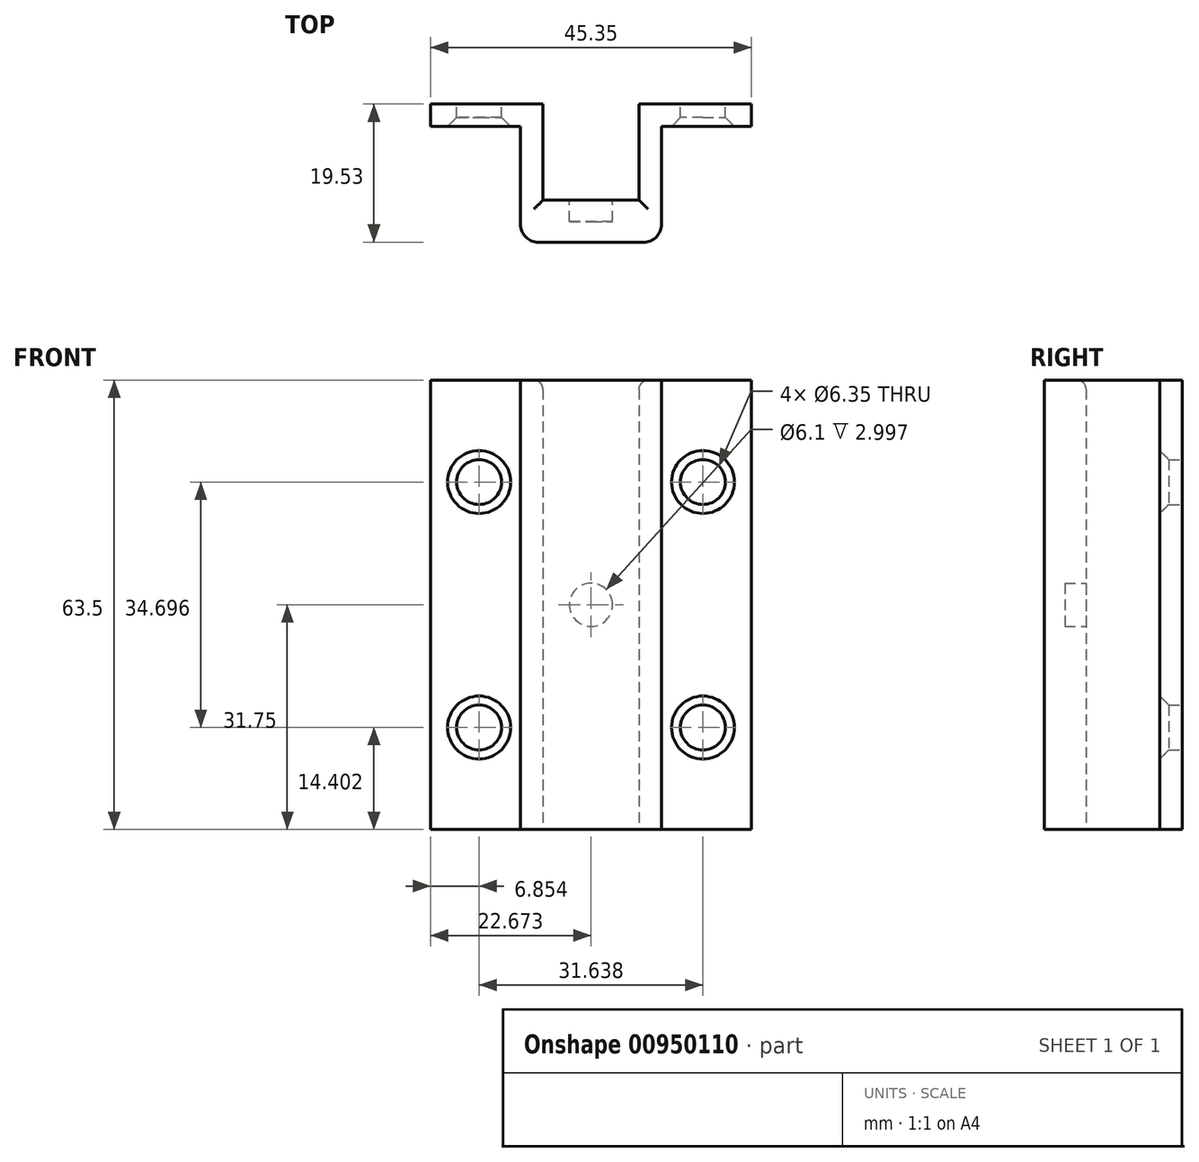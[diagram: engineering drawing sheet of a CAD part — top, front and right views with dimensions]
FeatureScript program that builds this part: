
annotation { "Feature Type Name" : "Feature", "Feature Type Description" : "" }
export const myFeature = defineFeature(function(context is Context, id is Id, definition is map)
    precondition{}
    {
        {
            var Q0;
            Q0=qCreatedBy(makeId("Top.planeOp"),FACE);
            var sketch = newSketch(context, id + "F0", { "sketchPlane" : qUnion([Q0])});
            skLineSegment(sketch, "E0", {"start": v(-9.03, 0) * mm, "end": v(4.58, 0) * mm});
            skLineSegment(sketch, "E1", {"start": v(-9.03, 0) * mm, "end": v(-9.03, 13.6) * mm});
            skLineSegment(sketch, "E2", {"start": v(4.58, 0) * mm, "end": v(4.58, 13.6) * mm});
            skLineSegment(sketch, "E3", {"start": v(4.58, 13.6) * mm, "end": v(20.45, 13.6) * mm});
            skLineSegment(sketch, "E4", {"start": v(20.45, 13.6) * mm, "end": v(20.45, 10.42) * mm});
            skLineSegment(sketch, "E5", {"start": v(20.45, 10.42) * mm, "end": v(7.75, 10.42) * mm});
            skLineSegment(sketch, "E6", {"start": v(7.75, 10.42) * mm, "end": v(7.75, -5.93) * mm});
            skLineSegment(sketch, "E7", {"start": v(7.75, -5.93) * mm, "end": v(-12.2, -5.93) * mm});
            skLineSegment(sketch, "E8", {"start": v(-9.03, 13.6) * mm, "end": v(-24.9, 13.6) * mm});
            skLineSegment(sketch, "E9", {"start": v(-24.9, 13.6) * mm, "end": v(-24.9, 10.42) * mm});
            skLineSegment(sketch, "E10", {"start": v(-24.9, 10.42) * mm, "end": v(-12.2, 10.42) * mm});
            skLineSegment(sketch, "E11", {"start": v(-12.2, 10.42) * mm, "end": v(-12.2, -5.93) * mm});
            skSolve(sketch);
        }
        {
            var Q0;
            Q0 = qSketchRegion(id + "F0", true);
            extrude(context, id + "F1", {"entities" : qUnion([Q0]), "depth" : 63.5 * mm, "offsetDistance" : 25.4 * mm});
        }
        {
            var Q0;
            Q0=makeQuery(id+"F1.opExtrude","SWEPT_FACE",FACE,{"disambiguationData":[OSD([sQuery(id+"F0.wireOp",EDGE,"E0")])]});
            var sketch = newSketch(context, id + "F2", { "sketchPlane" : qUnion([Q0])});
            skCircle(sketch, "E12", {"center": v(2.23, 31.75) * mm, "radius": 3.05 * mm});
            skPoint(sketch, "E13.orphan", {"position": v(-4.58, 31.75) * mm});
            skPoint(sketch, "E14.end.orphan", {"position": v(9.03, 31.75) * mm});
            skSolve(sketch);
        }
        {
            var Q0;
            Q0 = qSketchRegion(id + "F2", true);
            extrude(context, id + "F3", {"entities" : qUnion([Q0]), "operationType" : NewBodyOperationType.REMOVE, "oppositeDirection" : true, "depth" : 3 * mm, "offsetDistance" : 25.4 * mm});
        }
        {
            var Q0;
            Q0=makeQuery(id+"F1.opExtrude","SWEPT_FACE",FACE,{"disambiguationData":[OSD([sQuery(id+"F0.wireOp",EDGE,"E8")])]});
            var sketch = newSketch(context, id + "F4", { "sketchPlane" : qUnion([Q0])});
            skCircle(sketch, "E15", {"center": v(18.05, 49.1) * mm, "radius": 3.18 * mm});
            skCircle(sketch, "E16", {"center": v(18.05, 14.4) * mm, "radius": 3.18 * mm});
            skSolve(sketch);
        }
        {
            var Q0;
            Q0=makeQuery(id+"F1.opExtrude","SWEPT_FACE",FACE,{"disambiguationData":[OSD([sQuery(id+"F0.wireOp",EDGE,"E3")])]});
            var sketch = newSketch(context, id + "F5", { "sketchPlane" : qUnion([Q0])});
            skCircle(sketch, "E17", {"center": v(-13.6, 49.1) * mm, "radius": 3.18 * mm});
            skCircle(sketch, "E18", {"center": v(-13.6, 14.4) * mm, "radius": 3.18 * mm});
            skSolve(sketch);
        }
        {
            var Q0;
            Q0=makeQuery(id+"F5.imprint","IMPRINT",FACE,{"disambiguationData":[TD([[makeQuery(id+"F5.imprint","IMPRINT",EDGE,{"derivedFrom":sQuery(id+"F5.wireOp",EDGE,"E17")}),1.0]])]});
            var Q1;
            Q1=makeQuery(id+"F5.imprint","IMPRINT",FACE,{"disambiguationData":[TD([[makeQuery(id+"F5.imprint","IMPRINT",EDGE,{"derivedFrom":sQuery(id+"F5.wireOp",EDGE,"E18")}),1.0]])]});
            var Q2;
            Q2=makeQuery(id+"F4.imprint","IMPRINT",FACE,{"disambiguationData":[TD([[makeQuery(id+"F4.imprint","IMPRINT",EDGE,{"derivedFrom":sQuery(id+"F4.wireOp",EDGE,"E15")}),1.0]])]});
            var Q3;
            Q3=makeQuery(id+"F4.imprint","IMPRINT",FACE,{"disambiguationData":[TD([[makeQuery(id+"F4.imprint","IMPRINT",EDGE,{"derivedFrom":sQuery(id+"F4.wireOp",EDGE,"E16")}),1.0]])]});
            extrude(context, id + "F6", {"entities" : qUnion([Q0, Q1, Q2, Q3]), "operationType" : NewBodyOperationType.REMOVE, "oppositeDirection" : true, "depth" : 25.4 * mm, "offsetDistance" : 25.4 * mm});
        }
        {
            var Q0;
            Q0=makeQuery(id+"F6.boolean.opBoolean","INTERSECT",EDGE,{"derivedFrom":[makeQuery(id+"F1.opExtrude","SWEPT_FACE",FACE,{"disambiguationData":[OSD([sQuery(id+"F0.wireOp",EDGE,"E10")])]}),makeQuery(id+"F6.opExtrude","SWEPT_FACE",FACE,{"disambiguationData":[OSD([sQuery(id+"F4.wireOp",EDGE,"E15")])]})]});
            var Q1;
            Q1=makeQuery(id+"F6.boolean.opBoolean","INTERSECT",EDGE,{"derivedFrom":[makeQuery(id+"F1.opExtrude","SWEPT_FACE",FACE,{"disambiguationData":[OSD([sQuery(id+"F0.wireOp",EDGE,"E10")])]}),makeQuery(id+"F6.opExtrude","SWEPT_FACE",FACE,{"disambiguationData":[OSD([sQuery(id+"F4.wireOp",EDGE,"E16")])]})]});
            var Q2;
            Q2=makeQuery(id+"F6.boolean.opBoolean","INTERSECT",EDGE,{"derivedFrom":[makeQuery(id+"F1.opExtrude","SWEPT_FACE",FACE,{"disambiguationData":[OSD([sQuery(id+"F0.wireOp",EDGE,"E5")])]}),makeQuery(id+"F6.opExtrude","SWEPT_FACE",FACE,{"disambiguationData":[OSD([sQuery(id+"F5.wireOp",EDGE,"E17")])]})]});
            var Q3;
            Q3=makeQuery(id+"F6.boolean.opBoolean","INTERSECT",EDGE,{"derivedFrom":[makeQuery(id+"F1.opExtrude","SWEPT_FACE",FACE,{"disambiguationData":[OSD([sQuery(id+"F0.wireOp",EDGE,"E5")])]}),makeQuery(id+"F6.opExtrude","SWEPT_FACE",FACE,{"disambiguationData":[OSD([sQuery(id+"F5.wireOp",EDGE,"E18")])]})]});
            chamfer(context, id + "F7", {"entities" : qUnion([Q0, Q1, Q2, Q3]), "width" : 1.27 * mm, "tangentPropagation" : true});
        }
        {
            var Q0;
            Q0=makeQuery(id+"F1.opExtrude","SWEPT_EDGE",EDGE,{"disambiguationData":[OSD([sQuery(id+"F0.wireOp",EDGE,"E6"),sQuery(id+"F0.wireOp",EDGE,"E7")])]});
            var Q1;
            Q1=makeQuery(id+"F1.opExtrude","SWEPT_EDGE",EDGE,{"disambiguationData":[OSD([sQuery(id+"F0.wireOp",EDGE,"E7"),sQuery(id+"F0.wireOp",EDGE,"E11")])]});
            fillet(context, id + "F8", {"entities" : qUnion([Q0, Q1]), "radius" : 2.54 * mm, "tangentPropagation" : true, "allowEdgeOverflow" : false});
        }
        {
            var Q0;
            Q0=makeQuery(id+"F1.opExtrude","CAP_EDGE",EDGE,{"disambiguationData":[OSD([sQuery(id+"F0.wireOp",EDGE,"E1")])],"isStart":false});
            var Q1;
            Q1=makeQuery(id+"F1.opExtrude","CAP_EDGE",EDGE,{"disambiguationData":[OSD([sQuery(id+"F0.wireOp",EDGE,"E2")])],"isStart":false});
            var Q2;
            Q2=makeQuery(id+"F1.opExtrude","CAP_EDGE",EDGE,{"disambiguationData":[OSD([sQuery(id+"F0.wireOp",EDGE,"E0")])],"isStart":false});
            fillet(context, id + "F9", {"entities" : qUnion([Q0, Q1, Q2]), "radius" : 1.27 * mm, "tangentPropagation" : true, "allowEdgeOverflow" : false});
        }
    });
